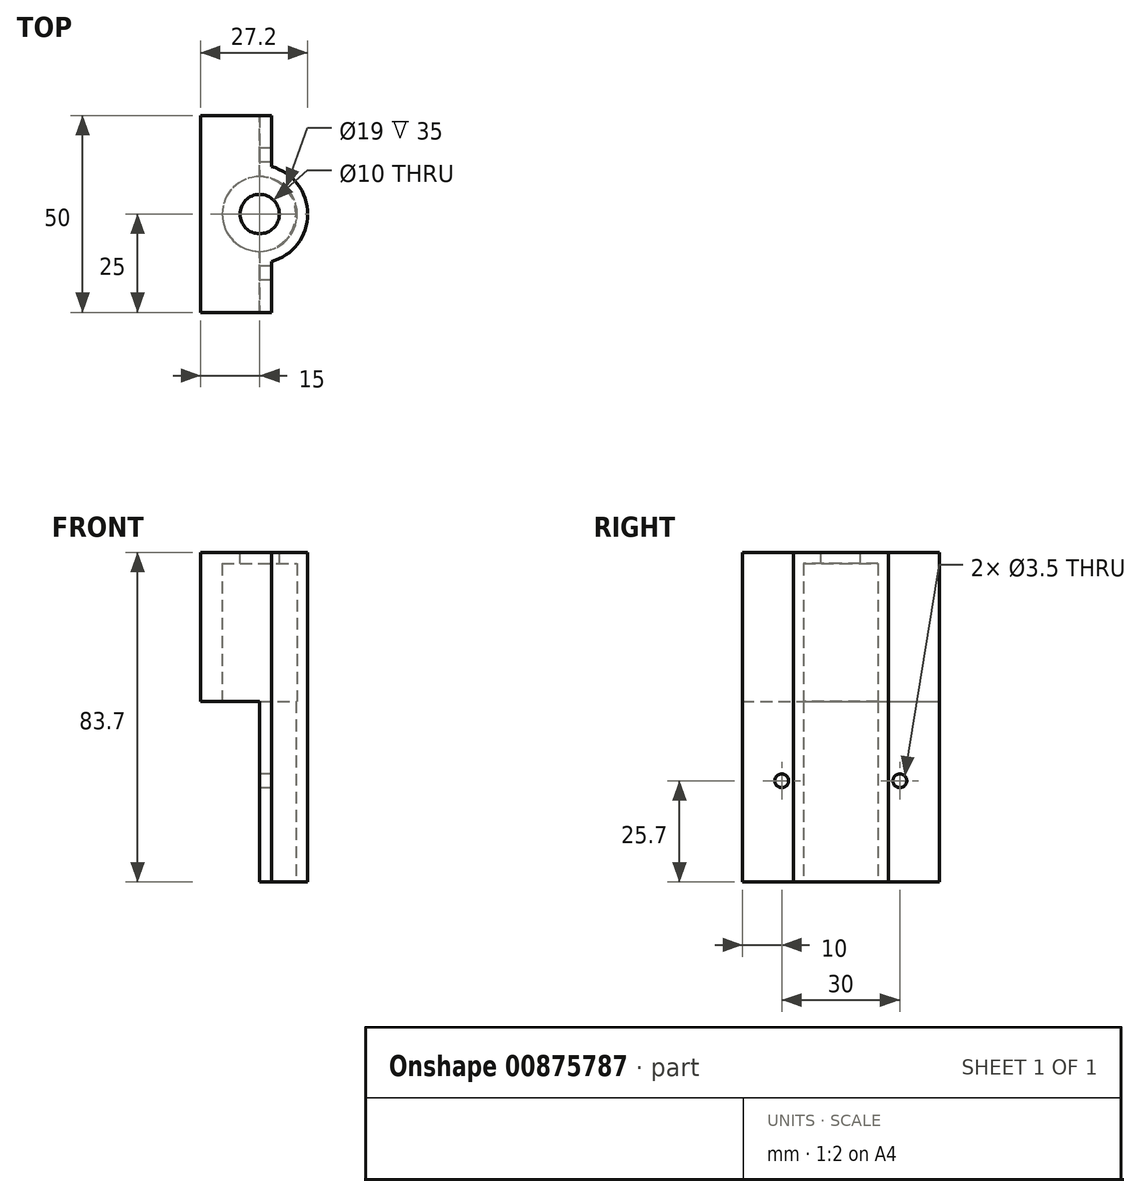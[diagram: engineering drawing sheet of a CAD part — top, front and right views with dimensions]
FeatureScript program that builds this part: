
annotation { "Feature Type Name" : "Feature", "Feature Type Description" : "" }
export const myFeature = defineFeature(function(context is Context, id is Id, definition is map)
    precondition{}
    {
        {
            var Q0;
            Q0=qCreatedBy(makeId("Right.planeOp"),FACE);
            var sketch = newSketch(context, id + "F0", { "sketchPlane" : qUnion([Q0])});
            skLineSegment(sketch, "E0", {"start": v(0, 0) * mm, "end": v(-25, 0) * mm});
            skLineSegment(sketch, "E1", {"start": v(-25, 0) * mm, "end": v(-25, 38) * mm});
            skLineSegment(sketch, "E2", {"start": v(-25, 38) * mm, "end": v(25, 38) * mm});
            skLineSegment(sketch, "E3", {"start": v(25, 38) * mm, "end": v(25, 0) * mm});
            skLineSegment(sketch, "E4", {"start": v(25, 0) * mm, "end": v(0, 0) * mm});
            skSolve(sketch);
        }
        {
            var Q0;
            Q0 = qSketchRegion(id + "F0", true);
            extrude(context, id + "F1", {"entities" : qUnion([Q0]), "depth" : 16 * mm, "offsetDistance" : 25 * mm});
        }
        {
            var Q0;
            Q0=makeQuery(id+"F1.opExtrude","SWEPT_FACE",FACE,{"disambiguationData":[OSD([sQuery(id+"F0.wireOp",EDGE,"E0"),sQuery(id+"F0.wireOp",EDGE,"E4")])]});
            var sketch = newSketch(context, id + "F2", { "sketchPlane" : qUnion([Q0])});
            skPoint(sketch, "E5.center.orphan", {"position": v(-0.3, 0) * mm});
            skCircle(sketch, "E6", {"center": v(-0.3, 0) * mm, "radius": 9.5 * mm});
            skSolve(sketch);
        }
        {
            var Q0;
            Q0 = qSketchRegion(id + "F2", true);
            extrude(context, id + "F3", {"entities" : qUnion([Q0]), "operationType" : NewBodyOperationType.REMOVE, "oppositeDirection" : true, "depth" : 35 * mm, "offsetDistance" : 25 * mm});
        }
        {
            var Q0;
            Q0=makeQuery(id+"F1.opExtrude","SWEPT_FACE",FACE,{"disambiguationData":[OSD([sQuery(id+"F0.wireOp",EDGE,"E0"),sQuery(id+"F0.wireOp",EDGE,"E4")])]});
            var sketch = newSketch(context, id + "F4", { "sketchPlane" : qUnion([Q0])});
            skLineSegment(sketch, "E7", {"start": v(0, 0) * mm, "end": v(0, 25) * mm, "construction": true});
            skLineSegment(sketch, "E8", {"start": v(0, 25) * mm, "end": v(3, 25) * mm, "construction": true});
            skLineSegment(sketch, "E9", {"start": v(3, 25) * mm, "end": v(3, 12.06) * mm});
            skPoint(sketch, "E9.endSnap0", {"position": v(8, -25) * mm});
            skPoint(sketch, "E10", {"position": v(3, 11.8) * mm});
            skPoint(sketch, "E11", {"position": v(3, -11.8) * mm});
            skLineSegment(sketch, "E12.trimOffspring", {"start": v(3, -12.06) * mm, "end": v(3, -25) * mm});
            skLineSegment(sketch, "E13", {"start": v(3, 25) * mm, "end": v(16, 25) * mm});
            skLineSegment(sketch, "E14", {"start": v(16, 25) * mm, "end": v(16, -25) * mm});
            skLineSegment(sketch, "E15", {"start": v(16, -25) * mm, "end": v(3, -25) * mm});
            skArc(sketch, "E16.0", {"start": v(3, -12.06) * mm, "mid": v(12.2, 0) * mm, "end": v(3, 12.06) * mm});
            skPoint(sketch, "E17", {"position": v(3, 12.06) * mm});
            skPoint(sketch, "E18", {"position": v(3, -12.06) * mm});
            skSolve(sketch);
        }
        {
            var Q0;
            Q0 = qSketchRegion(id + "F4", true);
            extrude(context, id + "F5", {"entities" : qUnion([Q0]), "operationType" : NewBodyOperationType.REMOVE, "oppositeDirection" : true, "depth" : 40 * mm, "offsetDistance" : 25 * mm});
        }
        {
            var Q0;
            Q0=makeQuery(id+"F1.opExtrude","SWEPT_FACE",FACE,{"disambiguationData":[OSD([sQuery(id+"F0.wireOp",EDGE,"E0"),sQuery(id+"F0.wireOp",EDGE,"E4")])]});
            extrude(context, id + "F6", {"entities" : qUnion([Q0]), "operationType" : NewBodyOperationType.ADD, "depth" : 45.7 * mm, "offsetDistance" : 25 * mm});
        }
        {
            var Q0;
            {var subQ0=sQuery(id+"F0.wireOp",EDGE,"E4");var subQ1=sQuery(id+"F0.wireOp",EDGE,"E3");var subQ2=sQuery(id+"F0.wireOp",EDGE,"E1");var subQ3=sQuery(id+"F0.wireOp",EDGE,"E0");var subQ4=makeQuery(id+"F1.opExtrude","CAP_FACE",FACE,{"disambiguationData":[OSD([subQ3,subQ2,sQuery(id+"F0.wireOp",EDGE,"E2"),subQ1,subQ0])],"isStart":true});var subQ7=makeQuery(id+"F1.opExtrude","CAP_EDGE",EDGE,{"disambiguationData":[OSD([subQ3,subQ0])],"isStart":true});Q0=makeQuery(id+"F6.boolean.opBoolean","MERGE",FACE,{"derivedFrom":[subQ4,makeQuery(id+"F6.opExtrude","SWEPT_FACE",FACE,{"disambiguationData":[OSD([subQ3,subQ0]),TDD([makeQuery(id+"F3.boolean.opBoolean","SPLIT",EDGE,{"disambiguationData":[TD([makeQuery(id+"F1.opExtrude","SWEPT_FACE",FACE,{"disambiguationData":[OSD([subQ2])]})])],"derivedFrom":subQ7})])]}),makeQuery(id+"F6.opExtrude","SWEPT_FACE",FACE,{"disambiguationData":[OSD([subQ3,subQ0]),TDD([makeQuery(id+"F3.boolean.opBoolean","SPLIT",EDGE,{"disambiguationData":[TD([makeQuery(id+"F1.opExtrude","SWEPT_FACE",FACE,{"disambiguationData":[OSD([subQ1])]})])],"derivedFrom":subQ7})])]})]});}
            var sketch = newSketch(context, id + "F7", { "sketchPlane" : qUnion([Q0])});
            skLineSegment(sketch, "E19.top", {"start": v(25, 38) * mm, "end": v(-25, 38) * mm});
            skPoint(sketch, "E19.left.start.orphan", {"position": v(25, 0) * mm});
            skLineSegment(sketch, "E20", {"start": v(25, 38) * mm, "end": v(25, 0.2) * mm});
            skLineSegment(sketch, "E21", {"start": v(25, 0.2) * mm, "end": v(-25, 0.2) * mm});
            skLineSegment(sketch, "E22", {"start": v(-25, 0.2) * mm, "end": v(-25, 38) * mm});
            skSolve(sketch);
        }
        {
            var Q0;
            Q0 = qSketchRegion(id + "F7", true);
            extrude(context, id + "F8", {"entities" : qUnion([Q0]), "operationType" : NewBodyOperationType.ADD, "depth" : 15 * mm, "offsetDistance" : 25 * mm});
        }
        {
            var Q0;
            Q0=makeQuery(id+"F8.opExtrude","SWEPT_FACE",FACE,{"disambiguationData":[OSD([sQuery(id+"F7.wireOp",EDGE,"E21")])]});
            var sketch = newSketch(context, id + "F9", { "sketchPlane" : qUnion([Q0])});
            skLineSegment(sketch, "E23", {"start": v(0, 0) * mm, "end": v(-0.3, 0) * mm, "construction": true});
            skCircle(sketch, "E24", {"center": v(0, 0) * mm, "radius": 9.5 * mm});
            skSolve(sketch);
        }
        {
            var Q0;
            Q0 = qSketchRegion(id + "F9", true);
            extrude(context, id + "F10", {"entities" : qUnion([Q0]), "operationType" : NewBodyOperationType.REMOVE, "oppositeDirection" : true, "depth" : 35 * mm, "offsetDistance" : 25 * mm});
        }
        {
            var Q0;
            Q0=makeQuery(id+"F8.boolean.opBoolean","MERGE",FACE,{"derivedFrom":[makeQuery(id+"F1.opExtrude","SWEPT_FACE",FACE,{"disambiguationData":[OSD([sQuery(id+"F0.wireOp",EDGE,"E2")])]}),makeQuery(id+"F8.opExtrude","SWEPT_FACE",FACE,{"disambiguationData":[OSD([sQuery(id+"F7.wireOp",EDGE,"E19.top")])]})]});
            var sketch = newSketch(context, id + "F11", { "sketchPlane" : qUnion([Q0])});
            skCircle(sketch, "E25", {"center": v(0, 0) * mm, "radius": 5 * mm});
            skLineSegment(sketch, "E26", {"start": v(0, 0) * mm, "end": v(0, 25) * mm, "construction": true});
            skLineSegment(sketch, "E27", {"start": v(0, 25) * mm, "end": v(-15, 25) * mm, "construction": true});
            skLineSegment(sketch, "E28", {"start": v(-15, 25) * mm, "end": v(3, 25) * mm, "construction": true});
            skSolve(sketch);
        }
        {
            var Q0;
            Q0 = qSketchRegion(id + "F11", true);
            extrude(context, id + "F12", {"entities" : qUnion([Q0]), "operationType" : NewBodyOperationType.REMOVE, "oppositeDirection" : true, "depth" : 25 * mm, "offsetDistance" : 25 * mm});
        }
        {
            var Q0;
            {var subQ0=sQuery(id+"F0.wireOp",EDGE,"E4");var subQ1=sQuery(id+"F0.wireOp",EDGE,"E3");var subQ4=makeQuery(id+"F1.opExtrude","SWEPT_FACE",FACE,{"disambiguationData":[OSD([subQ1])]});var subQ5=sQuery(id+"F0.wireOp",EDGE,"E0");var subQ8=sQuery(id+"F0.wireOp",EDGE,"E1");var subQ9=makeQuery(id+"F1.opExtrude","CAP_FACE",FACE,{"disambiguationData":[OSD([subQ5,subQ8,sQuery(id+"F0.wireOp",EDGE,"E2"),subQ1,subQ0])],"isStart":true});var subQ11=makeQuery(id+"F1.opExtrude","CAP_EDGE",EDGE,{"disambiguationData":[OSD([subQ5,subQ0])],"isStart":true});Q0=makeQuery(id+"F8.boolean.opBoolean","SPLIT",FACE,{"disambiguationData":[TD([subQ4])],"derivedFrom":makeQuery(id+"F6.boolean.opBoolean","MERGE",FACE,{"derivedFrom":[subQ9,makeQuery(id+"F6.opExtrude","SWEPT_FACE",FACE,{"disambiguationData":[OSD([subQ5,subQ0]),TDD([makeQuery(id+"F3.boolean.opBoolean","SPLIT",EDGE,{"disambiguationData":[TD([makeQuery(id+"F1.opExtrude","SWEPT_FACE",FACE,{"disambiguationData":[OSD([subQ8])]})])],"derivedFrom":subQ11})])]}),makeQuery(id+"F6.opExtrude","SWEPT_FACE",FACE,{"disambiguationData":[OSD([subQ5,subQ0]),TDD([makeQuery(id+"F3.boolean.opBoolean","SPLIT",EDGE,{"disambiguationData":[TD([subQ4])],"derivedFrom":subQ11})])]})]})});}
            var sketch = newSketch(context, id + "F13", { "sketchPlane" : qUnion([Q0])});
            skLineSegment(sketch, "E29", {"start": v(0, 0) * mm, "end": v(-15, 0) * mm, "construction": true});
            skLineSegment(sketch, "E30", {"start": v(-15, 0) * mm, "end": v(-15, -20) * mm, "construction": true});
            skCircle(sketch, "E31", {"center": v(-15, -20) * mm, "radius": 1.75 * mm});
            skLineSegment(sketch, "E32", {"start": v(0, 0) * mm, "end": v(0, -15) * mm, "construction": true});
            skCircle(sketch, "E33.MirrorC", {"center": v(15, -20) * mm, "radius": 1.75 * mm});
            skSolve(sketch);
        }
        {
            var Q0;
            Q0 = qSketchRegion(id + "F13", true);
            extrude(context, id + "F14", {"entities" : qUnion([Q0]), "operationType" : NewBodyOperationType.REMOVE, "oppositeDirection" : true, "depth" : 5 * mm, "offsetDistance" : 25 * mm});
        }
    });
